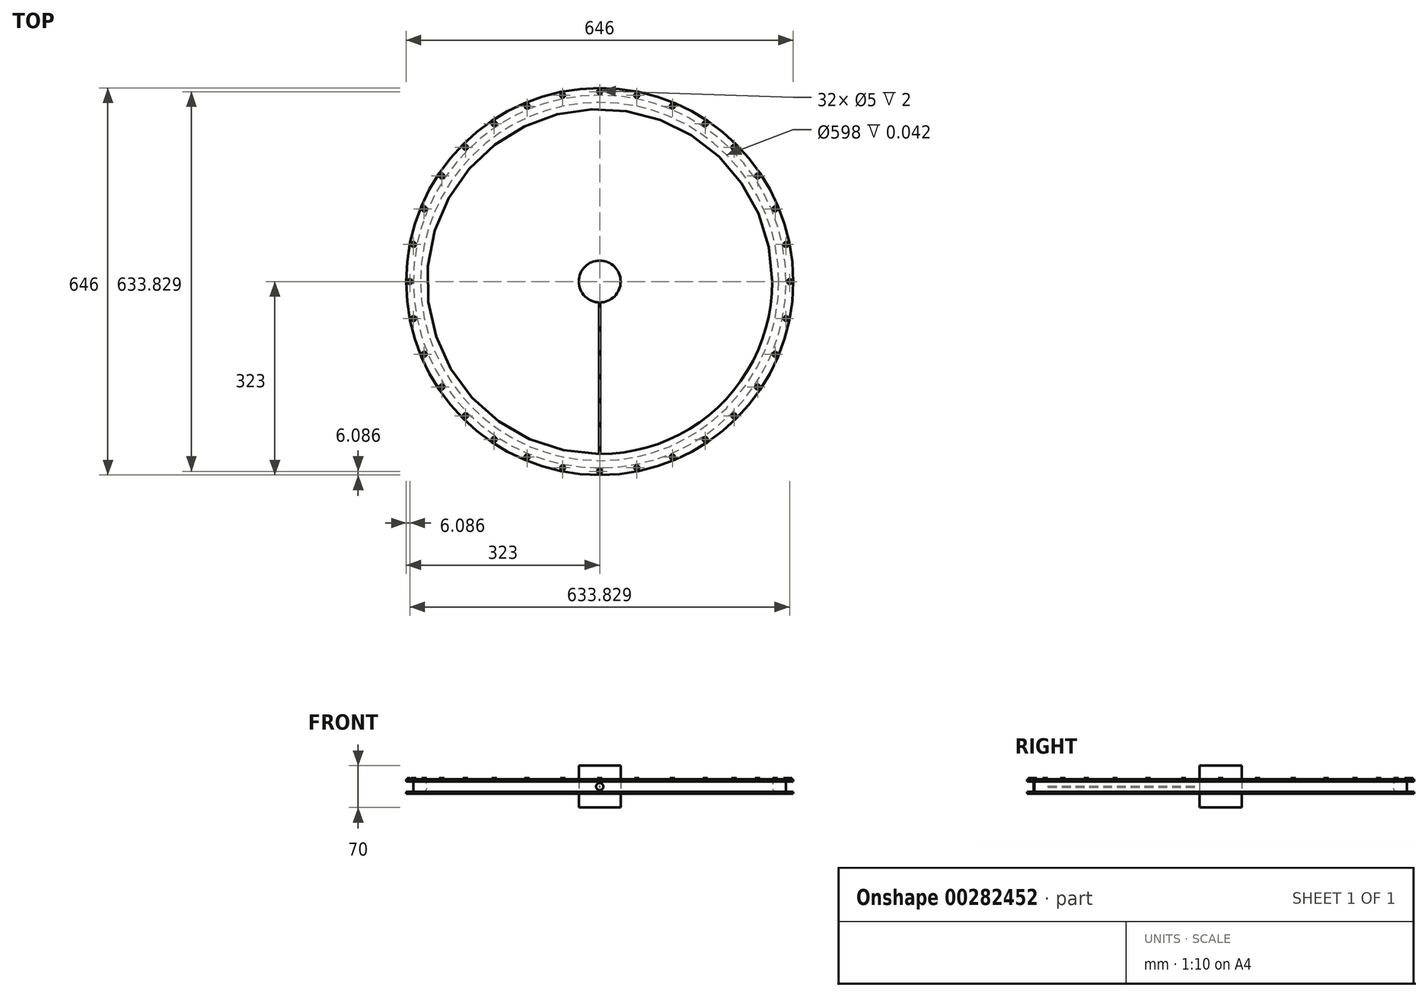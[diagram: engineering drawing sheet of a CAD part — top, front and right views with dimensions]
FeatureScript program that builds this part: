
annotation { "Feature Type Name" : "Feature", "Feature Type Description" : "" }
export const myFeature = defineFeature(function(context is Context, id is Id, definition is map)
    precondition{}
    {
        {
            var Q0;
            Q0=qCreatedBy(makeId("Top.planeOp"),FACE);
            var sketch = newSketch(context, id + "F0", { "sketchPlane" : qUnion([Q0])});
            skCircle(sketch, "E0", {"center": v(0, 0) * mm, "radius": 325 * mm});
            skCircle(sketch, "E1", {"center": v(0, 0) * mm, "radius": 300 * mm});
            skSolve(sketch);
        }
        {
            var Q0;
            Q0=qCreatedBy(makeId("Top.planeOp"),FACE);
            var sketch = newSketch(context, id + "F1", { "sketchPlane" : qUnion([Q0])});
            skCircle(sketch, "E2", {"center": v(0, 0) * mm, "radius": 35 * mm});
            skSolve(sketch);
        }
        {
            var Q0;
            Q0=makeQuery(id+"F1.imprint","IMPRINT",FACE,{"disambiguationData":[TD([[makeQuery(id+"F1.imprint","IMPRINT",EDGE,{"derivedFrom":sQuery(id+"F1.wireOp",EDGE,"E2")}),1.0]])]});
            extrude(context, id + "F2", {"entities" : qUnion([Q0]), "endBound" : BoundingType.SYMMETRIC, "depth" : 70 * mm});
        }
        {
            var Q0;
            Q0=qCreatedBy(makeId("Front.planeOp"),FACE);
            var sketch = newSketch(context, id + "F3", { "sketchPlane" : qUnion([Q0])});
            skLineSegment(sketch, "E3", {"start": v(0, 36.77) * mm, "end": v(0, -61.58) * mm});
            skLineSegment(sketch, "E4", {"start": v(-311, 33) * mm, "end": v(-311, -42.76) * mm});
            skLineSegment(sketch, "E5.bottom", {"start": v(-323, 12) * mm, "end": v(-299, 12) * mm});
            skLineSegment(sketch, "E5.top", {"start": v(-323, -12) * mm, "end": v(-299, -12) * mm});
            skLineSegment(sketch, "E5.left", {"start": v(-323, 12) * mm, "end": v(-323, 8.35) * mm});
            skLineSegment(sketch, "E5.right", {"start": v(-299, 12) * mm, "end": v(-299, 11.96) * mm});
            skPoint(sketch, "E5.middle", {"position": v(-311, 0) * mm});
            skLineSegment(sketch, "E6", {"start": v(-323, 8.35) * mm, "end": v(-311, 8.35) * mm});
            skLineSegment(sketch, "E7", {"start": v(-323, -8.68) * mm, "end": v(-311, -8.68) * mm});
            skArc(sketch, "E8", {"start": v(-300, -12) * mm, "mid": v(-288, 0) * mm, "end": v(-300, 12) * mm});
            skLineSegment(sketch, "E9.trimOffspring", {"start": v(-299, -11.96) * mm, "end": v(-299, -12) * mm});
            skLineSegment(sketch, "E10.trimOffspring", {"start": v(-323, -8.68) * mm, "end": v(-323, -12) * mm});
            skSolve(sketch);
        }
        {
            var Q0;
            {var subQ4=sQuery(id+"F3.wireOp",EDGE,"E5.left");Q0=makeQuery(id+"F3.imprint","IMPRINT",FACE,{"disambiguationData":[TD([[makeQuery(id+"F3.imprint","IMPRINT",EDGE,{"derivedFrom":subQ4}),1.0]])]});}
            var Q1;
            {var subQ0=sQuery(id+"F3.wireOp",EDGE,"E7");Q1=makeQuery(id+"F3.imprint","IMPRINT",FACE,{"disambiguationData":[TD([[makeQuery(id+"F3.imprint","IMPRINT",EDGE,{"derivedFrom":subQ0}),-1.0]])]});}
            var Q2;
            {var subQ0=sQuery(id+"F3.wireOp",EDGE,"E9.trimOffspring");Q2=makeQuery(id+"F3.imprint","IMPRINT",FACE,{"disambiguationData":[TD([[makeQuery(id+"F3.imprint","IMPRINT",EDGE,{"derivedFrom":subQ0}),-1.0]])]});}
            var Q3;
            {var subQ3=sQuery(id+"F3.wireOp",EDGE,"E4");var subQ11=makeQuery(id+"F3.imprint","INTERSECT",VERTEX,{"derivedFrom":[subQ3,sQuery(id+"F3.wireOp",EDGE,"E6")]});Q3=makeQuery(id+"F3.imprint","IMPRINT",FACE,{"disambiguationData":[TD([[makeQuery(id+"F3.imprint","IMPRINT",EDGE,{"disambiguationData":[TD([[subQ11,1.0]])],"derivedFrom":subQ3}),1.0]])]});}
            var Q4;
            Q4=sQuery(id+"F3.wireOp",EDGE,"E3");
            revolve(context, id + "F4", {"operationType" : NewBodyOperationType.ADD, "entities" : qUnion([Q0, Q1, Q2, Q3]), "axis" : qUnion([Q4]), "revolveType" : RevolveType.FULL});
        }
        {
            var Q0;
            Q0=makeQuery(id+"F4.opRevolve","SWEPT_FACE",FACE,{"disambiguationData":[OSD([sQuery(id+"F3.wireOp",EDGE,"E5.bottom")])]});
            var sketch = newSketch(context, id + "F5", { "sketchPlane" : qUnion([Q0])});
            skCircle(sketch, "E11", {"center": v(0, -316.91) * mm, "radius": 2.5 * mm});
            skCircle(sketch, "E12", {"center": v(0, -316.91) * mm, "radius": 4.05 * mm});
            skSolve(sketch);
        }
        {
            var Q0;
            Q0=makeQuery(id+"F5.imprint","IMPRINT",FACE,{"disambiguationData":[TD([[makeQuery(id+"F5.imprint","IMPRINT",EDGE,{"derivedFrom":sQuery(id+"F5.wireOp",EDGE,"E11")}),-1.0]])]});
            extrude(context, id + "F6", {"entities" : qUnion([Q0]), "operationType" : NewBodyOperationType.ADD, "depth" : 2 * mm});
        }
        {
            var Q0;
            Q0=makeQuery(id+"F4.opRevolve","SWEPT_BODY",BODY,{"disambiguationData":[OSD([sQuery(id+"F3.wireOp",EDGE,"E4"),sQuery(id+"F3.wireOp",EDGE,"E5.bottom"),sQuery(id+"F3.wireOp",EDGE,"E5.top"),sQuery(id+"F3.wireOp",EDGE,"E5.left"),sQuery(id+"F3.wireOp",EDGE,"E6"),sQuery(id+"F3.wireOp",EDGE,"E7"),sQuery(id+"F3.wireOp",EDGE,"E8"),sQuery(id+"F3.wireOp",EDGE,"E9.trimOffspring"),sQuery(id+"F3.wireOp",EDGE,"E10.trimOffspring")])]});
            var Q1;
            Q1=makeQuery(id+"F2.opExtrude","CAP_EDGE",EDGE,{"disambiguationData":[OSD([sQuery(id+"F1.wireOp",EDGE,"E2")])],"isStart":false});
            circularPattern(context, id + "F7", {"operationType" : NewBodyOperationType.ADD, "entities" : qUnion([Q0]), "axis" : qUnion([Q1]), "angle" : 360 * degree, "instanceCount" : 32, "equalSpace" : true});
        }
        {
            var Q0;
            Q0=qCreatedBy(makeId("Front.planeOp"),FACE);
            var sketch = newSketch(context, id + "F8", { "sketchPlane" : qUnion([Q0])});
            skCircle(sketch, "E13", {"center": v(0, 0) * mm, "radius": 1 * mm});
            skSolve(sketch);
        }
        {
            var Q0;
            Q0 = qSketchRegion(id + "F8", true);
            extrude(context, id + "F9", {"entities" : qUnion([Q0]), "operationType" : NewBodyOperationType.ADD, "depth" : 311.1 * mm});
        }
        {
            var Q0;
            Q0=makeQuery(id+"F9.opExtrude","CAP_FACE",FACE,{"disambiguationData":[OSD([sQuery(id+"F8.wireOp",EDGE,"E13")])],"isStart":false});
            var sketch = newSketch(context, id + "F10", { "sketchPlane" : qUnion([Q0])});
            skCircle(sketch, "E14", {"center": v(0, 0) * mm, "radius": 6 * mm});
            skSolve(sketch);
        }
        {
            var Q0;
            Q0 = qSketchRegion(id + "F10", true);
            extrude(context, id + "F11", {"entities" : qUnion([Q0]), "operationType" : NewBodyOperationType.ADD, "depth" : 1 * mm});
        }
    });
